# Revit family: 56252XXX
name_source: partatom
category: Plumbing Fixtures
revit_build: Autodesk Revit 2018 (Build: 20170223_1515(x64)
units: mm (PartAtom-declared; Revit-internal decimal feet)

## family parameters
Cut with Voids When Loaded = No
Host = Face
OmniClass Number = 23.31.17.29
OmniClass Title = Shower Drains
Part Type = Normal
Room Calculation Point = No
Round Connector Dimension = Use Diameter
Shared = No

## types (1)
- 800 Stainless Steel Optic
    Connector Description = Water Outlet 40 mm
    Default Elevation = 1219 mm
    Description = RainDrain Prism Complete set point drain 240/240 Nordics
    Diameter = 40 mm  [stored 0.131234 ft]
    Edition number = 0
    Manufacturer = Hansgrohe
    Material = Hansgrohe - Metal - 800 Stainless Steel Optic
    Material 1 = Hansgrohe - Plastic - Black
    Material 2 = Hansgrohe - Metal - Stainless Steel
    Model = 56252XXX
    Product Guid = 42d4d6d1-a6e9-47ac-811a-3b5fe29b9c0b
    Product Page URL = https://pro.hansgrohe.com
    Product data url = https://bimobject.com
    URL = https://www.hansgrohe.com
    Version = 1

note: [stored X ft] marks values corroborated as IEEE doubles in the binary element streams (Revit-internal decimal feet)

## geometry (parser evidence)
native form markers: Sweep x4
no freeform markers — native parametric forms only
